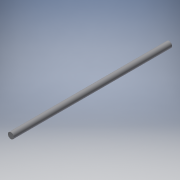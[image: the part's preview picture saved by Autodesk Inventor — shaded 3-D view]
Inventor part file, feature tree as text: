
AUTODESK INVENTOR PART (.ipt)
format: ipt  version: 2016 (Build 200138000, 138)  size: 87,552 bytes
history: native  units: in
note: dims shown in document units (in); Inventor stores cm internally (conversion verified against a paired STEP export)
features: sketch x2, extrude x1
ambient origin geometry x8: Origin, YZ Plane, XZ Plane, XY Plane, X Axis, Y Axis, Z Axis, Center Point
bodies: Solid1 (feature_tree)
feature tree (3):
  sketch  "Sketch1"  dims[d0=0.125in d1=3.3in d2=0.0in]
  extrude  "Extrusion1"  Depth=3.3in TaperAngle=0.0deg
  sketch  "Sketch2"
